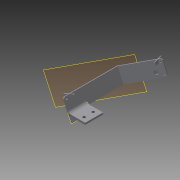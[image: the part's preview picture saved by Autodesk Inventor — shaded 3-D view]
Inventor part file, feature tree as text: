
AUTODESK INVENTOR PART (.ipt)
format: ipt  version: 2014 SP2 (Build 180247200, 247)  size: 269,824 bytes
history: native  units: mm
features: extrude x7, sketch x7, other x4, chamfer x3, projected_geometry x3
ambient origin geometry x8: Origin, YZ Plane, XZ Plane, XY Plane, X Axis, Y Axis, Z Axis, Center Point
bodies: Body1 (feature_tree)
feature tree (24):
  other  "camera-holder.ipt"
  extrude  "押し出し1"  Depth=10.0mm
  extrude  "押し出し2"  Depth=1.5mm TaperAngle=0.0deg
  extrude  "押し出し3"  Depth=1.5mm TaperAngle=0.0deg
  extrude  "押し出し4"  Depth=50.0mm TaperAngle=0.0deg
  extrude  "押し出し5"  Depth=50.0mm TaperAngle=0.0deg
  extrude  "押し出し6"  Depth=3.0mm
  chamfer  "面取り1"  Distance=3.0mm
  chamfer  "面取り2"  Distance=4.0mm
  chamfer  "面取り3"  Distance=2.0mm
  extrude  "押し出し7"  Depth=2.0mm
  other  "ソリッド2::camera-holder.ipt"
  other  "TaggingFeature1"
  sketch  "スケッチ21"
  sketch  "スケッチ22"
  sketch  "スケッチ3"
  sketch  "スケッチ4"
  sketch  "スケッチ5"
  sketch  "スケッチ6"
  projected_geometry  "投影ループ1"
  projected_geometry  "投影ループ2"
  sketch  "スケッチ7"
  projected_geometry  "投影ループ3"
  other  "ソリッド1"
